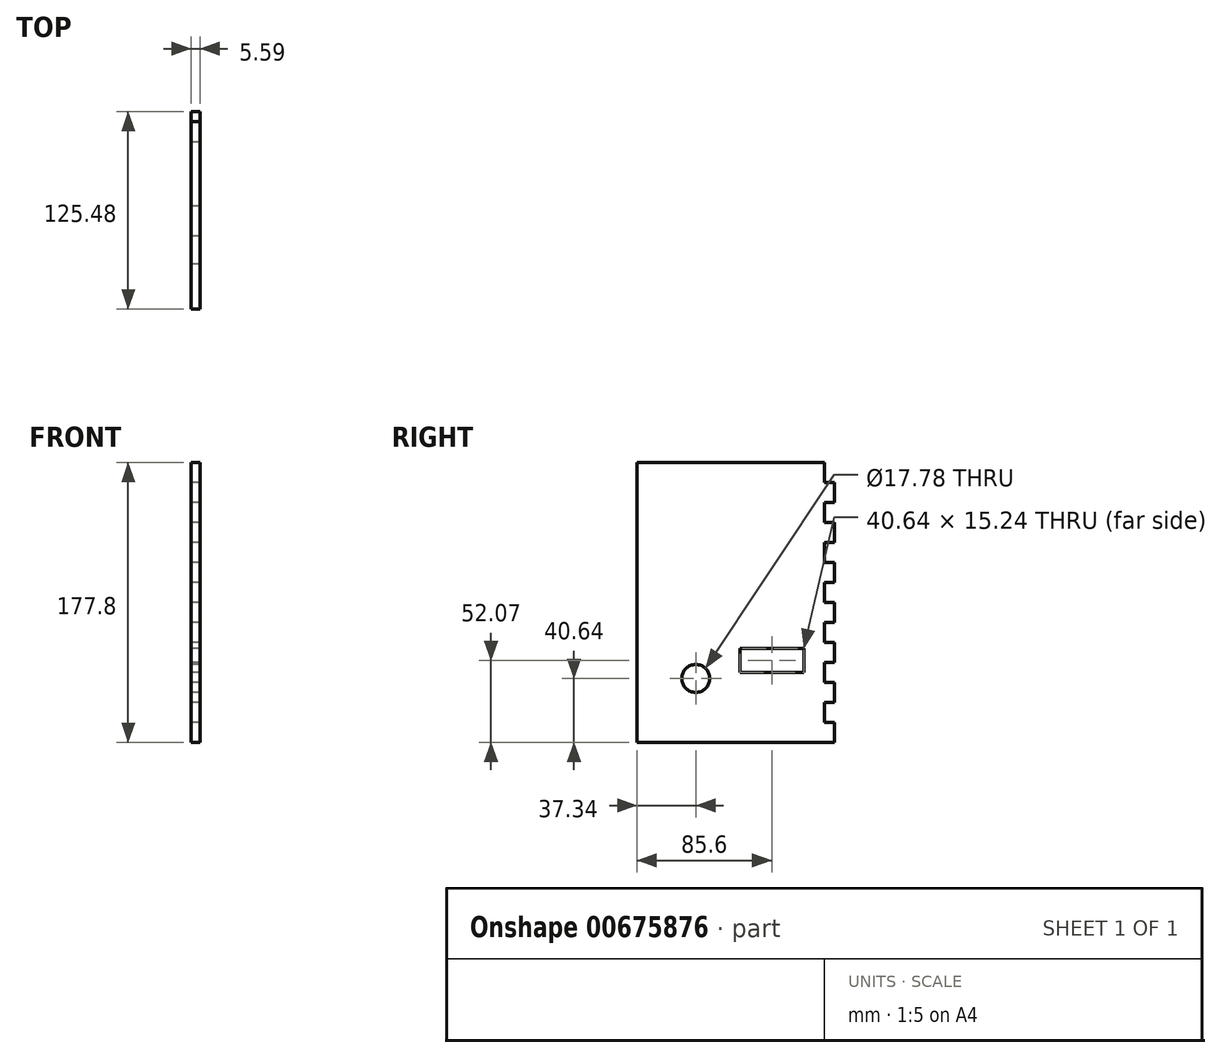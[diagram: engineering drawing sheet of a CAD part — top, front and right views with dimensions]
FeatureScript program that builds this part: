
annotation { "Feature Type Name" : "Feature", "Feature Type Description" : "" }
export const myFeature = defineFeature(function(context is Context, id is Id, definition is map)
    precondition{}
    {
        {
            var Q0;
            Q0=qCreatedBy(makeId("Right.planeOp"),FACE);
            var sketch = newSketch(context, id + "F0", { "sketchPlane" : qUnion([Q0])});
            skLineSegment(sketch, "E0.bottom", {"start": v(62.74, 88.9) * mm, "end": v(-62.74, 88.9) * mm});
            skLineSegment(sketch, "E0.top", {"start": v(62.74, -88.9) * mm, "end": v(-62.74, -88.9) * mm});
            skLineSegment(sketch, "E0.left", {"start": v(62.74, 88.9) * mm, "end": v(62.74, -88.9) * mm});
            skLineSegment(sketch, "E0.right", {"start": v(-62.74, 88.9) * mm, "end": v(-62.74, -88.9) * mm});
            skPoint(sketch, "E0.middle", {"position": v(0, 0) * mm});
            skSolve(sketch);
        }
        {
            var Q0;
            Q0 = qSketchRegion(id + "F0", true);
            extrude(context, id + "F1", {"entities" : qUnion([Q0]), "depth" : 5.6 * mm, "offsetDistance" : 25.4 * mm});
        }
        {
            var Q0;
            Q0=qCreatedBy(makeId("Right.planeOp"),FACE);
            var sketch = newSketch(context, id + "F2", { "sketchPlane" : qUnion([Q0])});
            skLineSegment(sketch, "E1.bottom", {"start": v(62.74, 88.9) * mm, "end": v(56.39, 88.9) * mm});
            skLineSegment(sketch, "E1.top", {"start": v(62.74, 76.2) * mm, "end": v(56.39, 76.2) * mm});
            skLineSegment(sketch, "E1.left", {"start": v(62.74, 88.9) * mm, "end": v(62.74, 76.2) * mm});
            skLineSegment(sketch, "E1.right", {"start": v(56.39, 88.9) * mm, "end": v(56.39, 76.2) * mm});
            skLineSegment(sketch, "E2.bottom", {"start": v(62.74, 63.5) * mm, "end": v(56.39, 63.5) * mm});
            skLineSegment(sketch, "E2.top", {"start": v(62.74, 50.8) * mm, "end": v(56.39, 50.8) * mm});
            skLineSegment(sketch, "E2.left", {"start": v(62.74, 63.5) * mm, "end": v(62.74, 50.8) * mm});
            skLineSegment(sketch, "E2.right", {"start": v(56.39, 63.5) * mm, "end": v(56.39, 50.8) * mm});
            skLineSegment(sketch, "E3.bottom", {"start": v(62.74, 38.1) * mm, "end": v(56.39, 38.1) * mm});
            skLineSegment(sketch, "E3.top", {"start": v(62.74, 25.4) * mm, "end": v(56.39, 25.4) * mm});
            skLineSegment(sketch, "E3.left", {"start": v(62.74, 38.1) * mm, "end": v(62.74, 25.4) * mm});
            skLineSegment(sketch, "E3.right", {"start": v(56.39, 38.1) * mm, "end": v(56.39, 25.4) * mm});
            skLineSegment(sketch, "E4.bottom", {"start": v(62.74, 12.7) * mm, "end": v(56.39, 12.7) * mm});
            skLineSegment(sketch, "E4.top", {"start": v(62.74, 0) * mm, "end": v(56.39, 0) * mm});
            skLineSegment(sketch, "E4.left", {"start": v(62.74, 12.7) * mm, "end": v(62.74, 0) * mm});
            skLineSegment(sketch, "E4.right", {"start": v(56.39, 12.7) * mm, "end": v(56.39, 0) * mm});
            skLineSegment(sketch, "E5.bottom", {"start": v(62.74, -12.7) * mm, "end": v(56.39, -12.7) * mm});
            skLineSegment(sketch, "E5.top", {"start": v(62.74, -25.4) * mm, "end": v(56.39, -25.4) * mm});
            skLineSegment(sketch, "E5.left", {"start": v(62.74, -12.7) * mm, "end": v(62.74, -25.4) * mm});
            skLineSegment(sketch, "E5.right", {"start": v(56.39, -12.7) * mm, "end": v(56.39, -25.4) * mm});
            skLineSegment(sketch, "E6.bottom", {"start": v(62.74, -38.1) * mm, "end": v(56.39, -38.1) * mm});
            skLineSegment(sketch, "E6.top", {"start": v(62.74, -50.8) * mm, "end": v(56.39, -50.8) * mm});
            skLineSegment(sketch, "E6.left", {"start": v(62.74, -38.1) * mm, "end": v(62.74, -50.8) * mm});
            skLineSegment(sketch, "E6.right", {"start": v(56.39, -38.1) * mm, "end": v(56.39, -50.8) * mm});
            skLineSegment(sketch, "E7.bottom", {"start": v(62.74, -63.5) * mm, "end": v(56.39, -63.5) * mm});
            skLineSegment(sketch, "E7.top", {"start": v(62.74, -76.2) * mm, "end": v(56.39, -76.2) * mm});
            skLineSegment(sketch, "E7.left", {"start": v(62.74, -63.5) * mm, "end": v(62.74, -76.2) * mm});
            skLineSegment(sketch, "E7.right", {"start": v(56.39, -63.5) * mm, "end": v(56.39, -76.2) * mm});
            skSolve(sketch);
        }
        {
            var Q0;
            Q0 = qSketchRegion(id + "F2", true);
            extrude(context, id + "F3", {"entities" : qUnion([Q0]), "operationType" : NewBodyOperationType.REMOVE, "depth" : 25.4 * mm, "offsetDistance" : 25.4 * mm});
        }
        {
            var Q0;
            Q0=qCreatedBy(makeId("Right.planeOp"),FACE);
            var sketch = newSketch(context, id + "F4", { "sketchPlane" : qUnion([Q0])});
            skCircle(sketch, "E8", {"center": v(-25.4, -48.26) * mm, "radius": 8.9 * mm});
            skSolve(sketch);
        }
        {
            var Q0;
            Q0 = qSketchRegion(id + "F4", true);
            extrude(context, id + "F5", {"entities" : qUnion([Q0]), "operationType" : NewBodyOperationType.REMOVE, "depth" : 25.4 * mm, "offsetDistance" : 25.4 * mm});
        }
        {
            var Q0;
            Q0=qCreatedBy(makeId("Right.planeOp"),FACE);
            var sketch = newSketch(context, id + "F6", { "sketchPlane" : qUnion([Q0])});
            skLineSegment(sketch, "E9.bottom", {"start": v(2.54, -44.45) * mm, "end": v(43.18, -44.45) * mm});
            skLineSegment(sketch, "E9.top", {"start": v(2.54, -29.21) * mm, "end": v(43.18, -29.21) * mm});
            skLineSegment(sketch, "E9.left", {"start": v(2.54, -44.45) * mm, "end": v(2.54, -29.21) * mm});
            skLineSegment(sketch, "E9.right", {"start": v(43.18, -44.45) * mm, "end": v(43.18, -29.21) * mm});
            skPoint(sketch, "E9.middle", {"position": v(22.86, -36.83) * mm});
            skSolve(sketch);
        }
        {
            var Q0;
            Q0 = qSketchRegion(id + "F6", true);
            extrude(context, id + "F7", {"entities" : qUnion([Q0]), "operationType" : NewBodyOperationType.REMOVE, "depth" : 25.4 * mm, "offsetDistance" : 25.4 * mm});
        }
    });
